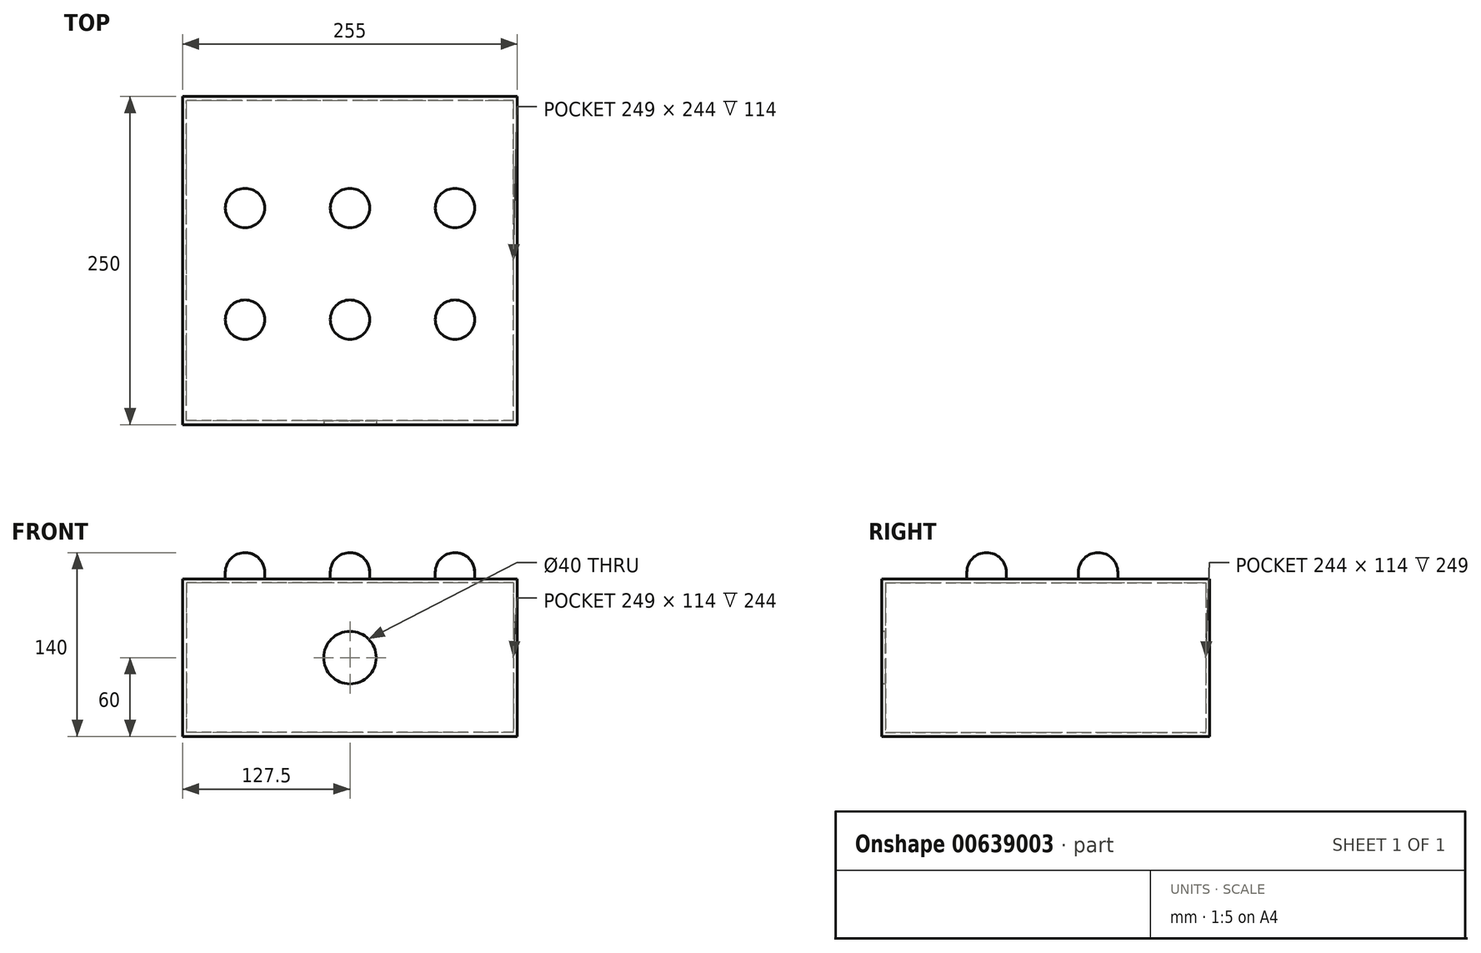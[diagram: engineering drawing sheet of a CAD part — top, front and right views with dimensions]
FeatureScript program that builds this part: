
annotation { "Feature Type Name" : "Feature", "Feature Type Description" : "" }
export const myFeature = defineFeature(function(context is Context, id is Id, definition is map)
    precondition{}
    {
        {
            var Q0;
            Q0=qCreatedBy(makeId("Top.planeOp"),FACE);
            var sketch = newSketch(context, id + "F0", { "sketchPlane" : qUnion([Q0])});
            skLineSegment(sketch, "E0.bottom", {"start": v(127.5, -125) * mm, "end": v(-127.5, -125) * mm});
            skLineSegment(sketch, "E0.top", {"start": v(127.5, 125) * mm, "end": v(-127.5, 125) * mm});
            skLineSegment(sketch, "E0.left", {"start": v(127.5, -125) * mm, "end": v(127.5, 125) * mm});
            skLineSegment(sketch, "E0.right", {"start": v(-127.5, -125) * mm, "end": v(-127.5, 125) * mm});
            skPoint(sketch, "E0.middle", {"position": v(0, 0) * mm});
            skSolve(sketch);
        }
        {
            var Q0;
            Q0=makeQuery(id+"F0.imprint","IMPRINT",FACE,{"disambiguationData":[TD([[makeQuery(id+"F0.imprint","IMPRINT",EDGE,{"derivedFrom":sQuery(id+"F0.wireOp",EDGE,"E0.bottom")}),-1.0]])]});
            extrude(context, id + "F1", {"entities" : qUnion([Q0]), "depth" : 117 * mm, "offsetDistance" : 25 * mm});
        }
        {
            var Q0;
            Q0=makeQuery(id+"F1.opExtrude","CAP_FACE",FACE,{"disambiguationData":[OSD([sQuery(id+"F0.wireOp",EDGE,"E0.bottom"),sQuery(id+"F0.wireOp",EDGE,"E0.top"),sQuery(id+"F0.wireOp",EDGE,"E0.left"),sQuery(id+"F0.wireOp",EDGE,"E0.right")])],"isStart":false});
            shell(context, id + "F2", {"entities" : qUnion([Q0]), "thickness" : 3 * mm});
        }
        {
            var Q0;
            Q0=makeQuery(id+"F1.opExtrude","CAP_FACE",FACE,{"disambiguationData":[OSD([sQuery(id+"F0.wireOp",EDGE,"E0.bottom"),sQuery(id+"F0.wireOp",EDGE,"E0.top"),sQuery(id+"F0.wireOp",EDGE,"E0.left"),sQuery(id+"F0.wireOp",EDGE,"E0.right")])],"isStart":false});
            var sketch = newSketch(context, id + "F3", { "sketchPlane" : qUnion([Q0])});
            skLineSegment(sketch, "E1.bottom", {"start": v(127.5, -125) * mm, "end": v(-127.5, -125) * mm});
            skLineSegment(sketch, "E1.top", {"start": v(127.5, 125) * mm, "end": v(-127.5, 125) * mm});
            skLineSegment(sketch, "E1.left", {"start": v(127.5, -125) * mm, "end": v(127.5, 125) * mm});
            skLineSegment(sketch, "E1.right", {"start": v(-127.5, -125) * mm, "end": v(-127.5, 125) * mm});
            skPoint(sketch, "E1.middle", {"position": v(0, 0) * mm});
            skSolve(sketch);
        }
        {
            var Q0;
            Q0 = qSketchRegion(id + "F3", true);
            extrude(context, id + "F4", {"entities" : qUnion([Q0]), "operationType" : NewBodyOperationType.ADD, "depth" : 3 * mm, "offsetDistance" : 25 * mm});
        }
        {
            var Q0;
            Q0=makeQuery(id+"F4.boolean.opBoolean","MERGE",FACE,{"derivedFrom":[makeQuery(id+"F1.opExtrude","SWEPT_FACE",FACE,{"disambiguationData":[OSD([sQuery(id+"F0.wireOp",EDGE,"E0.bottom")])]}),makeQuery(id+"F4.opExtrude","SWEPT_FACE",FACE,{"disambiguationData":[OSD([sQuery(id+"F3.wireOp",EDGE,"E1.bottom")])]})]});
            var sketch = newSketch(context, id + "F5", { "sketchPlane" : qUnion([Q0])});
            skCircle(sketch, "E2", {"center": v(0, 60) * mm, "radius": 20 * mm});
            skSolve(sketch);
        }
        {
            var Q0;
            Q0=makeQuery(id+"F5.imprint","IMPRINT",FACE,{"disambiguationData":[TD([[makeQuery(id+"F5.imprint","IMPRINT",EDGE,{"derivedFrom":sQuery(id+"F5.wireOp",EDGE,"E2")}),1.0]])]});
            var Q1;
            Q1=sQuery(id+"F5.wireOp",EDGE,"E2");
            extrude(context, id + "F6", {"entities" : qUnion([Q0]), "operationType" : NewBodyOperationType.REMOVE, "surfaceEntities" : qUnion([Q1]), "oppositeDirection" : true, "depth" : 25 * mm, "offsetDistance" : 25 * mm});
        }
        {
            var Q0;
            Q0=makeQuery(id+"F4.opExtrude","CAP_FACE",FACE,{"disambiguationData":[OSD([sQuery(id+"F3.wireOp",EDGE,"E1.bottom"),sQuery(id+"F3.wireOp",EDGE,"E1.top"),sQuery(id+"F3.wireOp",EDGE,"E1.left"),sQuery(id+"F3.wireOp",EDGE,"E1.right")])],"isStart":false});
            var sketch = newSketch(context, id + "F7", { "sketchPlane" : qUnion([Q0])});
            skCircle(sketch, "E3", {"center": v(-80, 40) * mm, "radius": 15 * mm});
            skCircle(sketch, "E4", {"center": v(0, 40) * mm, "radius": 15 * mm});
            skCircle(sketch, "E5", {"center": v(80, 40) * mm, "radius": 15 * mm});
            skCircle(sketch, "E6", {"center": v(-80, -45) * mm, "radius": 15 * mm});
            skCircle(sketch, "E7", {"center": v(0, -45) * mm, "radius": 15 * mm});
            skCircle(sketch, "E8", {"center": v(80, -45) * mm, "radius": 15 * mm});
            skPoint(sketch, "E9.orphan", {"position": v(127.5, 40) * mm});
            skPoint(sketch, "E10.start.orphan", {"position": v(-127.5, 40) * mm});
            skPoint(sketch, "E11.orphan", {"position": v(-127.5, -45) * mm});
            skPoint(sketch, "E12.end.orphan", {"position": v(127.5, -45) * mm});
            skSolve(sketch);
        }
        {
            var Q0;
            Q0 = qSketchRegion(id + "F7", true);
            extrude(context, id + "F8", {"entities" : qUnion([Q0]), "operationType" : NewBodyOperationType.ADD, "depth" : 20 * mm, "offsetDistance" : 25 * mm});
        }
        {
            var Q0;
            Q0=makeQuery(id+"F8.opExtrude","CAP_EDGE",EDGE,{"disambiguationData":[OSD([sQuery(id+"F7.wireOp",EDGE,"E4")])],"isStart":false});
            var Q1;
            Q1=makeQuery(id+"F8.opExtrude","CAP_EDGE",EDGE,{"disambiguationData":[OSD([sQuery(id+"F7.wireOp",EDGE,"E3")])],"isStart":false});
            var Q2;
            Q2=makeQuery(id+"F8.opExtrude","CAP_EDGE",EDGE,{"disambiguationData":[OSD([sQuery(id+"F7.wireOp",EDGE,"E5")])],"isStart":false});
            var Q3;
            Q3=makeQuery(id+"F8.opExtrude","CAP_EDGE",EDGE,{"disambiguationData":[OSD([sQuery(id+"F7.wireOp",EDGE,"E8")])],"isStart":false});
            var Q4;
            Q4=makeQuery(id+"F8.opExtrude","CAP_EDGE",EDGE,{"disambiguationData":[OSD([sQuery(id+"F7.wireOp",EDGE,"E7")])],"isStart":false});
            var Q5;
            Q5=makeQuery(id+"F8.opExtrude","CAP_EDGE",EDGE,{"disambiguationData":[OSD([sQuery(id+"F7.wireOp",EDGE,"E6")])],"isStart":false});
            fillet(context, id + "F9", {"entities" : qUnion([Q0, Q1, Q2, Q3, Q4, Q5]), "radius" : 15 * mm, "tangentPropagation" : true, "allowEdgeOverflow" : false});
        }
    });
